# Revit family: Casement_34_C_Side_Hung_Standard
name_source: partatom
category: Windows
revit_build: Autodesk Revit 2014 (Build: 20130308_1515(x64)
units: mm (PartAtom-declared; Revit-internal decimal feet)

## types (12) — shared parameters
All Available Glazing Numbers = The rows below list the available glazing materials for this window:
Aluminium Thickness = 1 mm  [stored 0.00328084 ft]
Bead SG Gap = 13 mm  [stored 0.0426509 ft]
Casement Dimension = 34 mm
Custom Sash Left Width = 554 mm  [stored 1.81759 ft]
Custom Sash Right Width = 554 mm  [stored 1.81759 ft]
DG Extrusion Start = 7 mm  [stored 0.0229659 ft]
DG Gasket Finish = Double Glazing Gasket Material
DG Thickness Calc = 4 mm  [stored 0.0131234 ft]
Default Sill Height = 800 mm  [stored 2.62467 ft]
Depth Bead = 20 mm  [stored 0.0656168 ft]
Depth Mullion = 35 mm
Description = Window 34mm, Type C side hung
Frame Center Offset = 17 mm
Limit Fixed Pane Width Max = 1500 mm  [stored 4.92126 ft]
Limit Fixed Pane Width Min = 200 mm  [stored 0.656168 ft]
Limit Sash Height Max = 1500 mm  [stored 4.92126 ft]
Limit Sash Height Min = 300 mm  [stored 0.984252 ft]
Limit Sash Width Max = 700 mm  [stored 2.29659 ft]
Limit Sash Width Min = 300 mm  [stored 0.984252 ft]
Limit Window Height Max = 1546 mm  [stored 5.07218 ft]
Limit Window Height Min = 346 mm
Limit Window Width Max = 2700 mm
Limit Window Width Min = 1400 mm
Manufacturer = Crealco
Max System DG One Piece Thickness = 4 mm  [stored 0.0131234 ft]
Max System DG Unit Thickness = 20 mm  [stored 0.0656168 ft]
Model = Casement 34
Offset Bead Center Reversed = 17 mm
Offset Fixed Panel Left = 600 mm  [stored 1.9685 ft]
Offset Mullion Left Side = 570 mm  [stored 1.87008 ft]
Offset Mullion Right Side = 570 mm  [stored 1.87008 ft]
Offset Sash Side = 23 mm  [stored 0.0754593 ft]
Offset Sash Top = 23 mm  [stored 0.0754593 ft]
Offset Window Exterior = 17 mm
SG Gasket Thickness = 6 mm  [stored 0.019685 ft]
Sash Center Offset = 14 mm  [stored 0.0459318 ft]
Sash Overlap = 7 mm  [stored 0.0229659 ft]
Sash Spacing Inner = 8 mm  [stored 0.0262467 ft]
Side Hung Left = Yes
Side Hung Right = No
URL = http://www.crealco.co.za
Wall Closure = By host
Width Bead = 15 mm  [stored 0.0492126 ft]
Width Profile = 30 mm  [stored 0.0984252 ft]
Width Sash Left = 554 mm  [stored 1.81759 ft]
Width Sash Left Opening = 524 mm  [stored 1.71916 ft]
Width Sash Right = 554 mm  [stored 1.81759 ft]
Width Sash Right Opening = 524 mm  [stored 1.71916 ft]
zero-valued in all types: Window Exterior Offset

## per-type parameters (varying)
- 34-1809SS-1000Pa: Area Pane Left=0.35 m²; Area Pane Middle=0.48 m²; Area Pane Right=0.35 m²; Clearvue Insulated LowE SHGC Value=0.496; Clearvue Insulated LowE U Value=3.44; Clearvue Insulated U Value=4.06; Clearvue SHGC Value=0.614; Clearvue U Value=6.11; Custom Windload=1000 mm  [stored 3.28084 ft]; Custom Window Height=890 mm  [stored 2.91995 ft]; Custom Window Width=1790 mm; Energy Advantage SHGC Value=0.55; Energy Advantage U Value=4.64; Height=890 mm  [stored 2.91995 ft]; Height Fixed Panel Center=830 mm  [stored 2.7231 ft]; Height Sash=814 mm  [stored 2.6706 ft]; Height Sash Opening=844 mm  [stored 2.76903 ft]; Intruderprufe LowE SHGC Value=0.514; Intruderprufe LowE U Value=4.48; Intruderprufe SHGC Value=0.58; Intruderprufe U Value=6.07; Length Mullion=890 mm  [stored 2.91995 ft]; Max Pane Area=0.48 m²; Mullion Depth Windload Based=35 mm; Sash Height=845 mm  [stored 2.77231 ft]; Width=1790 mm; Width Fixed Panel Center=590 mm  [stored 1.9357 ft]; Windload Design=1000 mm  [stored 3.28084 ft]
- 34-1809SS-1500Pa: Area Pane Left=0.35 m²; Area Pane Middle=0.48 m²; Area Pane Right=0.35 m²; Clearvue Insulated LowE SHGC Value=0.496; Clearvue Insulated LowE U Value=3.44; Clearvue Insulated U Value=4.06; Clearvue SHGC Value=0.614; Clearvue U Value=6.11; Custom Windload=1500 mm  [stored 4.92126 ft]; Custom Window Height=890 mm  [stored 2.91995 ft]; Custom Window Width=1790 mm; Energy Advantage SHGC Value=0.55; Energy Advantage U Value=4.64; Height=890 mm  [stored 2.91995 ft]; Height Fixed Panel Center=830 mm  [stored 2.7231 ft]; Height Sash=814 mm  [stored 2.6706 ft]; Height Sash Opening=844 mm  [stored 2.76903 ft]; Intruderprufe LowE SHGC Value=0.514; Intruderprufe LowE U Value=4.48; Intruderprufe SHGC Value=0.58; Intruderprufe U Value=6.07; Length Mullion=890 mm  [stored 2.91995 ft]; Max Pane Area=0.48 m²; Mullion Depth Windload Based=35 mm; Sash Height=845 mm  [stored 2.77231 ft]; Width=1790 mm; Width Fixed Panel Center=590 mm  [stored 1.9357 ft]; Windload Design=1500 mm  [stored 4.92126 ft]
- 34-1809SS-2000Pa: Area Pane Left=0.35 m²; Area Pane Middle=0.48 m²; Area Pane Right=0.35 m²; Clearvue Insulated LowE SHGC Value=0.496; Clearvue Insulated LowE U Value=3.44; Clearvue Insulated U Value=4.06; Clearvue SHGC Value=0.614; Clearvue U Value=6.11; Custom Windload=2000 mm; Custom Window Height=890 mm  [stored 2.91995 ft]; Custom Window Width=1790 mm; Energy Advantage SHGC Value=0.55; Energy Advantage U Value=4.64; Height=890 mm  [stored 2.91995 ft]; Height Fixed Panel Center=830 mm  [stored 2.7231 ft]; Height Sash=814 mm  [stored 2.6706 ft]; Height Sash Opening=844 mm  [stored 2.76903 ft]; Intruderprufe LowE SHGC Value=0.514; Intruderprufe LowE U Value=4.48; Intruderprufe SHGC Value=0.58; Intruderprufe U Value=6.07; Length Mullion=890 mm  [stored 2.91995 ft]; Max Pane Area=0.48 m²; Mullion Depth Windload Based=35 mm; Sash Height=845 mm  [stored 2.77231 ft]; Width=1790 mm; Width Fixed Panel Center=590 mm  [stored 1.9357 ft]; Windload Design=2000 mm
- 34-2409SS-1000Pa: Area Pane Left=0.35 m²; Area Pane Middle=0.97 m²; Area Pane Right=0.35 m²; Clearvue Insulated LowE SHGC Value=0.525; Clearvue Insulated LowE U Value=3.2; Clearvue Insulated U Value=3.84; Clearvue SHGC Value=0.651; Clearvue U Value=6.07; Custom Windload=1000 mm  [stored 3.28084 ft]; Custom Window Height=890 mm  [stored 2.91995 ft]; Custom Window Width=2390 mm; Energy Advantage SHGC Value=0.583; Energy Advantage U Value=4.49; Height=890 mm  [stored 2.91995 ft]; Height Fixed Panel Center=830 mm  [stored 2.7231 ft]; Height Sash=814 mm  [stored 2.6706 ft]; Height Sash Opening=844 mm  [stored 2.76903 ft]; Intruderprufe LowE SHGC Value=0.544; Intruderprufe LowE U Value=4.3; Intruderprufe SHGC Value=0.615; Intruderprufe U Value=6; Length Mullion=890 mm  [stored 2.91995 ft]; Max Pane Area=0.97 m²; Mullion Depth Windload Based=35 mm; Sash Height=845 mm  [stored 2.77231 ft]; Width=2390 mm; Width Fixed Panel Center=1190 mm  [stored 3.9042 ft]; Windload Design=1000 mm  [stored 3.28084 ft]
- 34-2409SS-1500Pa: Area Pane Left=0.35 m²; Area Pane Middle=0.97 m²; Area Pane Right=0.35 m²; Clearvue Insulated LowE SHGC Value=0.525; Clearvue Insulated LowE U Value=3.2; Clearvue Insulated U Value=3.84; Clearvue SHGC Value=0.651; Clearvue U Value=6.07; Custom Windload=1500 mm  [stored 4.92126 ft]; Custom Window Height=890 mm  [stored 2.91995 ft]; Custom Window Width=2390 mm; Energy Advantage SHGC Value=0.583; Energy Advantage U Value=4.49; Height=890 mm  [stored 2.91995 ft]; Height Fixed Panel Center=830 mm  [stored 2.7231 ft]; Height Sash=814 mm  [stored 2.6706 ft]; Height Sash Opening=844 mm  [stored 2.76903 ft]; Intruderprufe LowE SHGC Value=0.544; Intruderprufe LowE U Value=4.3; Intruderprufe SHGC Value=0.615; Intruderprufe U Value=6; Length Mullion=890 mm  [stored 2.91995 ft]; Max Pane Area=0.97 m²; Mullion Depth Windload Based=35 mm; Sash Height=845 mm  [stored 2.77231 ft]; Width=2390 mm; Width Fixed Panel Center=1190 mm  [stored 3.9042 ft]; Windload Design=1500 mm  [stored 4.92126 ft]
- 34-2409SS-2000Pa: Area Pane Left=0.35 m²; Area Pane Middle=0.97 m²; Area Pane Right=0.35 m²; Clearvue Insulated LowE SHGC Value=0.525; Clearvue Insulated LowE U Value=3.2; Clearvue Insulated U Value=3.84; Clearvue SHGC Value=0.651; Clearvue U Value=6.07; Custom Windload=2000 mm; Custom Window Height=890 mm  [stored 2.91995 ft]; Custom Window Width=2390 mm; Energy Advantage SHGC Value=0.583; Energy Advantage U Value=4.49; Height=890 mm  [stored 2.91995 ft]; Height Fixed Panel Center=830 mm  [stored 2.7231 ft]; Height Sash=814 mm  [stored 2.6706 ft]; Height Sash Opening=844 mm  [stored 2.76903 ft]; Intruderprufe LowE SHGC Value=0.544; Intruderprufe LowE U Value=4.3; Intruderprufe SHGC Value=0.615; Intruderprufe U Value=6; Length Mullion=890 mm  [stored 2.91995 ft]; Max Pane Area=0.97 m²; Mullion Depth Windload Based=35 mm; Sash Height=845 mm  [stored 2.77231 ft]; Width=2390 mm; Width Fixed Panel Center=1190 mm  [stored 3.9042 ft]; Windload Design=2000 mm
- 34-1812SS-1000Pa: Area Pane Left=0.49 m²; Area Pane Middle=0.65 m²; Area Pane Right=0.49 m²; Clearvue Insulated LowE SHGC Value=0.514; Clearvue Insulated LowE U Value=3.3; Clearvue Insulated U Value=3.95; Clearvue SHGC Value=0.637; Clearvue U Value=6.09; Custom Windload=1000 mm  [stored 3.28084 ft]; Custom Window Height=1190 mm  [stored 3.9042 ft]; Custom Window Width=1790 mm; Energy Advantage SHGC Value=0.571; Energy Advantage U Value=4.55; Height=1190 mm  [stored 3.9042 ft]; Height Fixed Panel Center=1130 mm  [stored 3.70735 ft]; Height Sash=1114 mm  [stored 3.65486 ft]; Height Sash Opening=1144 mm; Intruderprufe LowE SHGC Value=0.533; Intruderprufe LowE U Value=4.41; Intruderprufe SHGC Value=0.603; Intruderprufe U Value=6.05; Length Mullion=1190 mm  [stored 3.9042 ft]; Max Pane Area=0.65 m²; Mullion Depth Windload Based=35 mm; Sash Height=1145 mm  [stored 3.75656 ft]; Width=1790 mm; Width Fixed Panel Center=590 mm  [stored 1.9357 ft]; Windload Design=1000 mm  [stored 3.28084 ft]
- 34-1812SS-1500Pa: Area Pane Left=0.49 m²; Area Pane Middle=0.65 m²; Area Pane Right=0.49 m²; Clearvue Insulated LowE SHGC Value=0.516; Clearvue Insulated LowE U Value=3.46; Clearvue Insulated U Value=3.84; Clearvue SHGC Value=0.638; Clearvue U Value=6.19; Custom Windload=1500 mm  [stored 4.92126 ft]; Custom Window Height=1190 mm  [stored 3.9042 ft]; Custom Window Width=1790 mm; Energy Advantage SHGC Value=0.572; Energy Advantage U Value=4.67; Height=1190 mm  [stored 3.9042 ft]; Height Fixed Panel Center=1130 mm  [stored 3.70735 ft]; Height Sash=1114 mm  [stored 3.65486 ft]; Height Sash Opening=1144 mm; Intruderprufe LowE SHGC Value=0.536; Intruderprufe LowE U Value=4.53; Intruderprufe SHGC Value=0.6; Intruderprufe U Value=5.83; Length Mullion=1190 mm  [stored 3.9042 ft]; Max Pane Area=0.65 m²; Mullion Depth Windload Based=54 mm  [stored 0.177165 ft]; Sash Height=1145 mm  [stored 3.75656 ft]; Width=1790 mm; Width Fixed Panel Center=590 mm  [stored 1.9357 ft]; Windload Design=1500 mm  [stored 4.92126 ft]
- 34-1812SS-2000Pa: Area Pane Left=0.49 m²; Area Pane Middle=0.65 m²; Area Pane Right=0.49 m²; Clearvue Insulated LowE SHGC Value=0.516; Clearvue Insulated LowE U Value=3.46; Clearvue Insulated U Value=3.84; Clearvue SHGC Value=0.638; Clearvue U Value=6.19; Custom Windload=2000 mm; Custom Window Height=1190 mm  [stored 3.9042 ft]; Custom Window Width=1790 mm; Energy Advantage SHGC Value=0.572; Energy Advantage U Value=4.67; Height=1190 mm  [stored 3.9042 ft]; Height Fixed Panel Center=1130 mm  [stored 3.70735 ft]; Height Sash=1114 mm  [stored 3.65486 ft]; Height Sash Opening=1144 mm; Intruderprufe LowE SHGC Value=0.536; Intruderprufe LowE U Value=4.53; Intruderprufe SHGC Value=0.6; Intruderprufe U Value=5.83; Length Mullion=1190 mm  [stored 3.9042 ft]; Max Pane Area=0.65 m²; Mullion Depth Windload Based=54 mm  [stored 0.177165 ft]; Sash Height=1145 mm  [stored 3.75656 ft]; Width=1790 mm; Width Fixed Panel Center=590 mm  [stored 1.9357 ft]; Windload Design=2000 mm
- 34-2412SS-1000Pa: Area Pane Left=0.49 m²; Area Pane Middle=1.32 m²; Area Pane Right=0.49 m²; Clearvue Insulated LowE SHGC Value=0.544; Clearvue Insulated LowE U Value=3.18; Clearvue Insulated U Value=3.65; Clearvue SHGC Value=0.674; Clearvue U Value=6.13; Custom Windload=1000 mm  [stored 3.28084 ft]; Custom Window Height=1190 mm  [stored 3.9042 ft]; Custom Window Width=2390 mm; Energy Advantage SHGC Value=0.604; Energy Advantage U Value=4.49; Height=1190 mm  [stored 3.9042 ft]; Height Fixed Panel Center=1130 mm  [stored 3.70735 ft]; Height Sash=1114 mm  [stored 3.65486 ft]; Height Sash Opening=1144 mm; Intruderprufe LowE SHGC Value=0.565; Intruderprufe LowE U Value=4.33; Intruderprufe SHGC Value=0.636; Intruderprufe U Value=5.82; Length Mullion=1190 mm  [stored 3.9042 ft]; Max Pane Area=1.32 m²; Mullion Depth Windload Based=54 mm  [stored 0.177165 ft]; Sash Height=1145 mm  [stored 3.75656 ft]; Width=2390 mm; Width Fixed Panel Center=1190 mm  [stored 3.9042 ft]; Windload Design=1000 mm  [stored 3.28084 ft]
- 34-2412SS-1500Pa: Area Pane Left=0.49 m²; Area Pane Middle=1.32 m²; Area Pane Right=0.49 m²; Clearvue Insulated LowE SHGC Value=0.544; Clearvue Insulated LowE U Value=3.18; Clearvue Insulated U Value=3.65; Clearvue SHGC Value=0.674; Clearvue U Value=6.13; Custom Windload=1500 mm  [stored 4.92126 ft]; Custom Window Height=1190 mm  [stored 3.9042 ft]; Custom Window Width=2390 mm; Energy Advantage SHGC Value=0.604; Energy Advantage U Value=4.49; Height=1190 mm  [stored 3.9042 ft]; Height Fixed Panel Center=1130 mm  [stored 3.70735 ft]; Height Sash=1114 mm  [stored 3.65486 ft]; Height Sash Opening=1144 mm; Intruderprufe LowE SHGC Value=0.565; Intruderprufe LowE U Value=4.33; Intruderprufe SHGC Value=0.636; Intruderprufe U Value=5.82; Length Mullion=1190 mm  [stored 3.9042 ft]; Max Pane Area=1.32 m²; Mullion Depth Windload Based=54 mm  [stored 0.177165 ft]; Sash Height=1145 mm  [stored 3.75656 ft]; Width=2390 mm; Width Fixed Panel Center=1190 mm  [stored 3.9042 ft]; Windload Design=1500 mm  [stored 4.92126 ft]
- 34-2412SS-2000Pa: Area Pane Left=0.49 m²; Area Pane Middle=1.32 m²; Area Pane Right=0.49 m²; Clearvue Insulated LowE SHGC Value=0.544; Clearvue Insulated LowE U Value=3.18; Clearvue Insulated U Value=3.65; Clearvue SHGC Value=0.674; Clearvue U Value=6.13; Custom Windload=2000 mm; Custom Window Height=1190 mm  [stored 3.9042 ft]; Custom Window Width=2390 mm; Energy Advantage SHGC Value=0.604; Energy Advantage U Value=4.49; Height=1190 mm  [stored 3.9042 ft]; Height Fixed Panel Center=1130 mm  [stored 3.70735 ft]; Height Sash=1114 mm  [stored 3.65486 ft]; Height Sash Opening=1144 mm; Intruderprufe LowE SHGC Value=0.565; Intruderprufe LowE U Value=4.33; Intruderprufe SHGC Value=0.636; Intruderprufe U Value=5.82; Length Mullion=1190 mm  [stored 3.9042 ft]; Max Pane Area=1.32 m²; Mullion Depth Windload Based=54 mm  [stored 0.177165 ft]; Sash Height=1145 mm  [stored 3.75656 ft]; Width=2390 mm; Width Fixed Panel Center=1190 mm  [stored 3.9042 ft]; Windload Design=2000 mm

note: [stored X ft] marks values corroborated as IEEE doubles in the binary element streams (Revit-internal decimal feet)

## geometry (parser evidence)
native form markers: Extrusion x1, Sweep x29
no freeform markers — native parametric forms only
